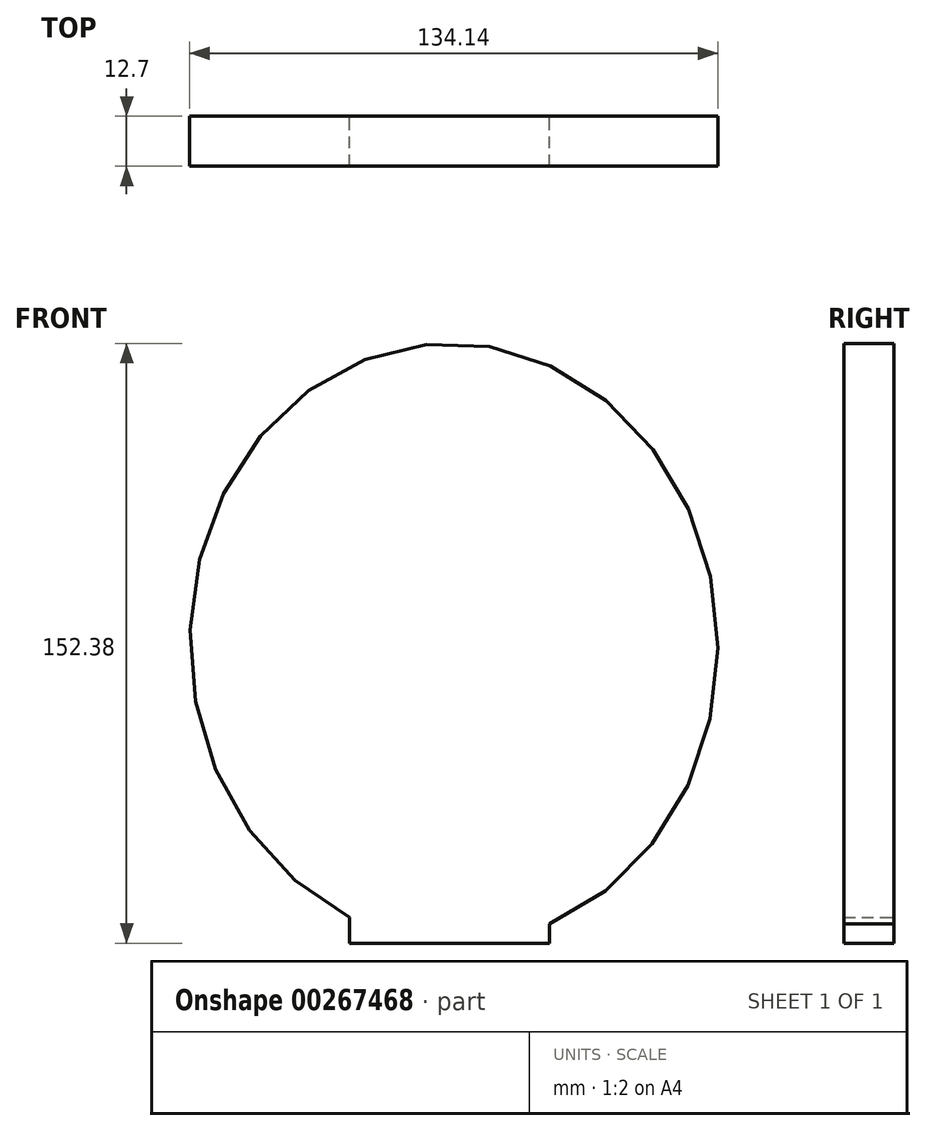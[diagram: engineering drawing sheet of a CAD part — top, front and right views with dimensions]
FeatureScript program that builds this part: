
annotation { "Feature Type Name" : "Feature", "Feature Type Description" : "" }
export const myFeature = defineFeature(function(context is Context, id is Id, definition is map)
    precondition{}
    {
        {
            var Q0;
            Q0=qCreatedBy(makeId("Front.planeOp"),FACE);
            var sketch = newSketch(context, id + "F0", { "sketchPlane" : qUnion([Q0])});
            skEllipse(sketch, "E0", {"center": v(0, 0) * mm, "majorRadius": 76.2 * mm, "minorRadius": 67.05 * mm, "majorAxis": v(-0.05, 1)});
            skSolve(sketch);
        }
        {
            var Q0;
            Q0 = qSketchRegion(id + "F0", true);
            extrude(context, id + "F1", {"entities" : qUnion([Q0]), "depth" : 12.7 * mm});
        }
        {
            var Q0;
            Q0=qCreatedBy(makeId("Top.planeOp"),FACE);
            var sketch = newSketch(context, id + "F2", { "sketchPlane" : qUnion([Q0])});
            skLineSegment(sketch, "E1.bottom", {"start": v(-26.43, 0) * mm, "end": v(24.37, 0) * mm});
            skLineSegment(sketch, "E1.top", {"start": v(-26.43, -12.7) * mm, "end": v(24.37, -12.7) * mm});
            skLineSegment(sketch, "E1.left", {"start": v(-26.43, 0) * mm, "end": v(-26.43, -12.7) * mm});
            skLineSegment(sketch, "E1.right", {"start": v(24.37, 0) * mm, "end": v(24.37, -12.7) * mm});
            skSolve(sketch);
        }
        {
            var Q0;
            Q0 = qSketchRegion(id + "F2", true);
            extrude(context, id + "F3", {"entities" : qUnion([Q0]), "operationType" : NewBodyOperationType.ADD, "oppositeDirection" : true, "depth" : 76.2 * mm});
        }
    });
